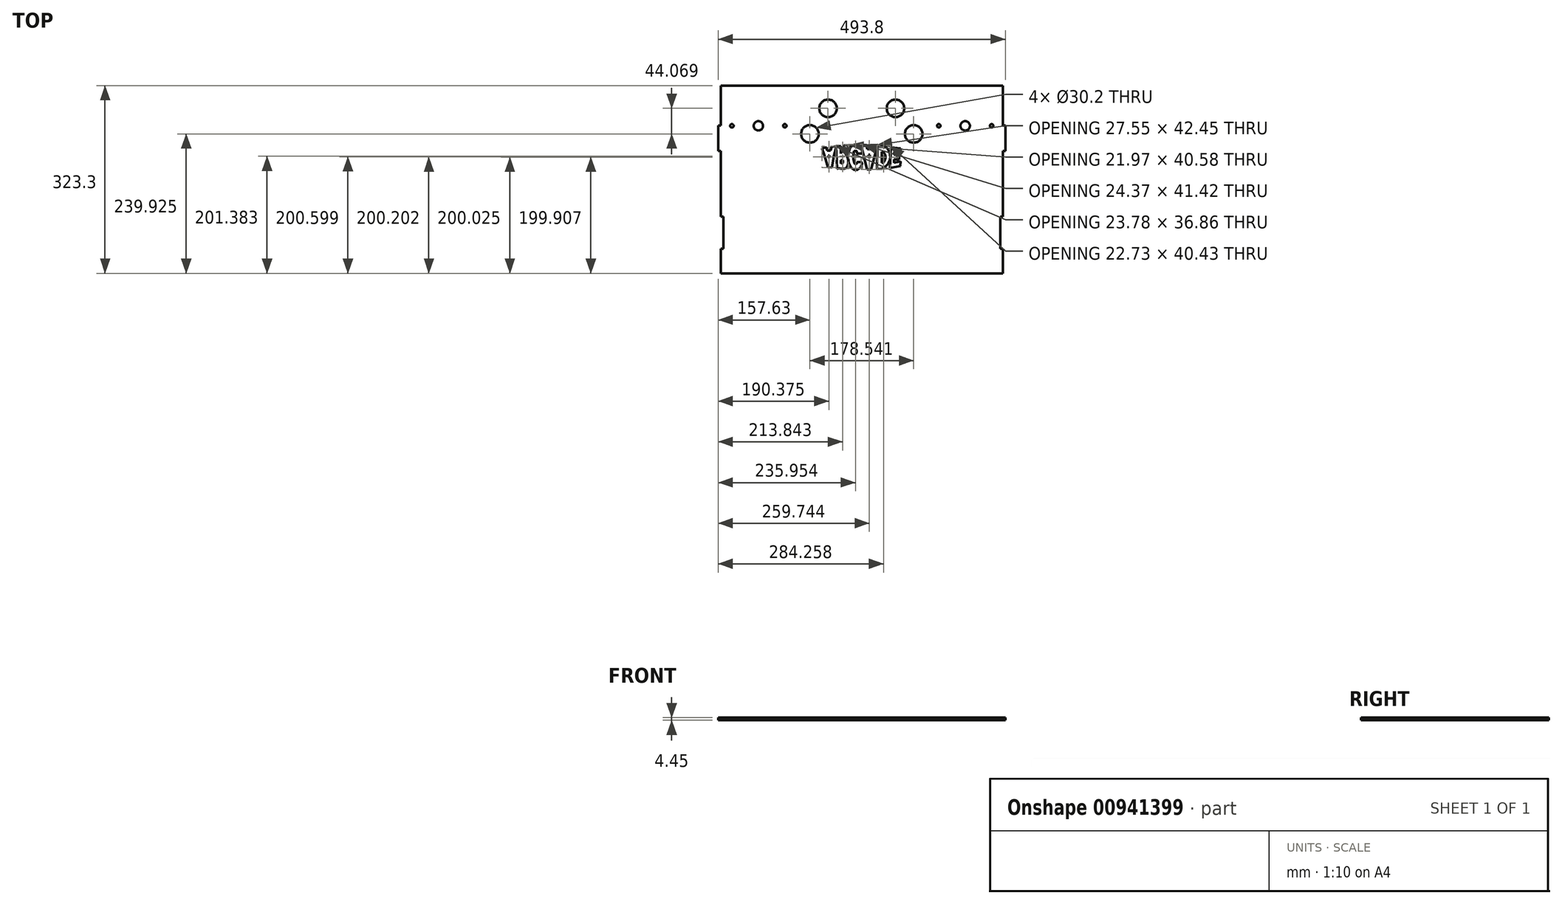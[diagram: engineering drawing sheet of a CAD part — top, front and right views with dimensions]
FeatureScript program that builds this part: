
annotation { "Feature Type Name" : "Feature", "Feature Type Description" : "" }
export const myFeature = defineFeature(function(context is Context, id is Id, definition is map)
    precondition{}
    {
        {
            var Q0;
            Q0=qCreatedBy(makeId("Top.planeOp"),FACE);
            var sketch = newSketch(context, id + "F0", { "sketchPlane" : qUnion([Q0])});
            skLineSegment(sketch, "E0.left", {"start": v(238, -33.63) * mm, "end": v(238, 22.07) * mm});
            skPoint(sketch, "E0.middle", {"position": v(0, 0) * mm});
            skLineSegment(sketch, "E1.bottom", {"start": v(238, 75.7) * mm, "end": v(242.45, 75.7) * mm});
            skLineSegment(sketch, "E1.top", {"start": v(238, 22.07) * mm, "end": v(242.45, 22.07) * mm});
            skLineSegment(sketch, "E1.right", {"start": v(242.45, 75.7) * mm, "end": v(242.45, 22.07) * mm});
            skLineSegment(sketch, "E2.bottom", {"start": v(238, -75.7) * mm, "end": v(242.45, -75.7) * mm});
            skLineSegment(sketch, "E2.top", {"start": v(238, -33.63) * mm, "end": v(242.45, -33.63) * mm});
            skLineSegment(sketch, "E2.right", {"start": v(242.45, -75.7) * mm, "end": v(242.45, -33.63) * mm});
            skLineSegment(sketch, "E3.left", {"start": v(238, 22.07) * mm, "end": v(238, -28.25) * mm});
            skLineSegment(sketch, "E4.MirrorCS", {"start": v(-242.45, -75.7) * mm, "end": v(-242.45, -33.63) * mm});
            skLineSegment(sketch, "E5.MirrorCS", {"start": v(-242.45, 75.7) * mm, "end": v(-242.45, 22.07) * mm});
            skLineSegment(sketch, "E6.MirrorCS", {"start": v(-238, 22.07) * mm, "end": v(-242.45, 22.07) * mm});
            skLineSegment(sketch, "E7.MirrorCS", {"start": v(-238, -33.63) * mm, "end": v(-238, 22.07) * mm});
            skLineSegment(sketch, "E8.MirrorCS", {"start": v(-238, -33.63) * mm, "end": v(-242.45, -33.63) * mm});
            skLineSegment(sketch, "E9.MirrorCS", {"start": v(-238, -75.7) * mm, "end": v(-242.45, -75.7) * mm});
            skLineSegment(sketch, "E10.MirrorCS", {"start": v(-238, 75.7) * mm, "end": v(-242.45, 75.7) * mm});
            skLineSegment(sketch, "E11.top", {"start": v(-232.45, 247.6) * mm, "end": v(232.45, 247.6) * mm});
            skLineSegment(sketch, "E11.left", {"start": v(-242.45, 75.7) * mm, "end": v(-242.45, 134.6) * mm});
            skLineSegment(sketch, "E11.right", {"start": v(242.45, 75.7) * mm, "end": v(242.45, 134.6) * mm});
            skPoint(sketch, "E12.visualSharp", {"position": v(-242.45, 247.6) * mm});
            skPoint(sketch, "E13.visualSharp", {"position": v(242.45, 247.6) * mm});
            skCircle(sketch, "E14", {"center": v(-223.33, 178.2) * mm, "radius": 3 * mm});
            skCircle(sketch, "E15", {"center": v(-132.43, 178.2) * mm, "radius": 3 * mm});
            skCircle(sketch, "E16", {"center": v(-89.27, 164.22) * mm, "radius": 15.1 * mm});
            skCircle(sketch, "E17", {"center": v(-58.02, 208.3) * mm, "radius": 15.1 * mm});
            skCircle(sketch, "E18.MirrorC", {"center": v(132.43, 178.2) * mm, "radius": 3 * mm});
            skCircle(sketch, "E19.MirrorC", {"center": v(223.33, 178.2) * mm, "radius": 3 * mm});
            skCircle(sketch, "E20.MirrorC", {"center": v(58.02, 208.3) * mm, "radius": 15.1 * mm});
            skCircle(sketch, "E21.MirrorC", {"center": v(89.27, 164.22) * mm, "radius": 15.1 * mm});
            skLineSegment(sketch, "E22.bottom", {"start": v(246.9, 134.6) * mm, "end": v(242.45, 134.6) * mm});
            skLineSegment(sketch, "E22.top", {"start": v(246.9, 178.7) * mm, "end": v(242.45, 178.7) * mm});
            skLineSegment(sketch, "E22.left", {"start": v(246.9, 134.6) * mm, "end": v(246.9, 178.7) * mm});
            skPoint(sketch, "E22.middle", {"position": v(242.45, 156.65) * mm});
            skPoint(sketch, "E22.right.start.orphan", {"position": v(238, 134.6) * mm});
            skLineSegment(sketch, "E23.trimOffspring", {"start": v(242.45, 178.7) * mm, "end": v(242.45, 237.6) * mm});
            skPoint(sketch, "E24.trimOffspring.end.orphan", {"position": v(238, 178.7) * mm});
            skLineSegment(sketch, "E25", {"start": v(-242.45, 237.6) * mm, "end": v(-242.45, 247.6) * mm});
            skLineSegment(sketch, "E26", {"start": v(-232.45, 247.6) * mm, "end": v(-242.45, 247.6) * mm});
            skLineSegment(sketch, "E27", {"start": v(232.45, 247.6) * mm, "end": v(242.45, 247.6) * mm});
            skLineSegment(sketch, "E28", {"start": v(242.45, 237.6) * mm, "end": v(242.45, 247.6) * mm});
            skLineSegment(sketch, "E29.MirrorCS", {"start": v(-246.9, 134.6) * mm, "end": v(-246.9, 178.7) * mm});
            skLineSegment(sketch, "E30.MirrorCS", {"start": v(-246.9, 134.6) * mm, "end": v(-242.45, 134.6) * mm});
            skLineSegment(sketch, "E31.MirrorCS", {"start": v(-246.9, 178.7) * mm, "end": v(-242.45, 178.7) * mm});
            skLineSegment(sketch, "E32.trimOffspring", {"start": v(-242.45, 178.7) * mm, "end": v(-242.45, 237.6) * mm});
            skLineSegment(sketch, "E33", {"start": v(-223.33, 178.2) * mm, "end": v(-220.33, 178.2) * mm});
            skCircle(sketch, "E34", {"center": v(-177.88, 178.2) * mm, "radius": 8.09 * mm});
            skLineSegment(sketch, "E35.trimOffspring", {"start": v(-135.43, 178.2) * mm, "end": v(-132.43, 178.2) * mm});
            skCircle(sketch, "E36.MirrorC", {"center": v(177.88, 178.2) * mm, "radius": 8.09 * mm});
            skLineSegment(sketch, "E37.MirrorCS", {"start": v(-36.17, 119.2) * mm, "end": v(-33.2, 119.2) * mm});
            skLineSegment(sketch, "E38.MirrorCS", {"start": v(26.62, 143.73) * mm, "end": v(26.56, 144.42) * mm});
            skLineSegment(sketch, "E39.MirrorCS", {"start": v(-0.93, 145.55) * mm, "end": v(-0.93, 145) * mm});
            skLineSegment(sketch, "E40.MirrorCS", {"start": v(-0.53, 145.55) * mm, "end": v(-0.93, 145.55) * mm});
            skLineSegment(sketch, "E41.MirrorCS", {"start": v(-32.23, 115.87) * mm, "end": v(-32.53, 114.75) * mm});
            skLineSegment(sketch, "E42.MirrorCS", {"start": v(-35.97, 113.5) * mm, "end": v(-36.17, 119.2) * mm});
            skLineSegment(sketch, "E43.MirrorCS", {"start": v(-32.1, 117.62) * mm, "end": v(-32.23, 115.87) * mm});
            skLineSegment(sketch, "E44.MirrorCS", {"start": v(-33.2, 119.2) * mm, "end": v(-32.1, 117.62) * mm});
            skLineSegment(sketch, "E45.MirrorCS", {"start": v(-33.2, 113.84) * mm, "end": v(-35.97, 113.5) * mm});
            skLineSegment(sketch, "E46.MirrorCS", {"start": v(-32.53, 114.75) * mm, "end": v(-33.2, 113.84) * mm});
            skLineSegment(sketch, "E47.MirrorCS", {"start": v(-23.7, 120.7) * mm, "end": v(-23.63, 120.17) * mm});
            skLineSegment(sketch, "E48.MirrorCS", {"start": v(-60.29, 140.96) * mm, "end": v(-60.29, 138.53) * mm});
            skLineSegment(sketch, "E49.MirrorCS", {"start": v(-53.54, 135.83) * mm, "end": v(-52.35, 139.61) * mm});
            skLineSegment(sketch, "E50.MirrorCS", {"start": v(-52.35, 139.61) * mm, "end": v(-52.35, 141.88) * mm});
            skLineSegment(sketch, "E51.MirrorCS", {"start": v(-60.29, 138.53) * mm, "end": v(-59.7, 135.3) * mm});
            skLineSegment(sketch, "E52.MirrorCS", {"start": v(-59.7, 135.3) * mm, "end": v(-53.54, 135.83) * mm});
            skLineSegment(sketch, "E53.MirrorCS", {"start": v(-44.64, 140.15) * mm, "end": v(-44.64, 143.33) * mm});
            skLineSegment(sketch, "E54.MirrorCS", {"start": v(-27.9, 128.28) * mm, "end": v(-26.01, 126.06) * mm});
            skLineSegment(sketch, "E55.MirrorCS", {"start": v(-44.64, 143.33) * mm, "end": v(-52.35, 141.88) * mm});
            skLineSegment(sketch, "E56.MirrorCS", {"start": v(14.2, 128.31) * mm, "end": v(12.9, 122.55) * mm});
            skLineSegment(sketch, "E57.MirrorCS", {"start": v(55.58, 128.77) * mm, "end": v(64.18, 127.53) * mm});
            skLineSegment(sketch, "E58.MirrorCS", {"start": v(27.1, 144.42) * mm, "end": v(38.2, 143.73) * mm});
            skLineSegment(sketch, "E59.MirrorCS", {"start": v(8.88, 103.1) * mm, "end": v(15.8, 103.1) * mm});
            skLineSegment(sketch, "E60.MirrorCS", {"start": v(-31.26, 144.14) * mm, "end": v(-22.07, 144.8) * mm});
            skLineSegment(sketch, "E61.MirrorCS", {"start": v(66.58, 116.97) * mm, "end": v(66.01, 108.94) * mm});
            skLineSegment(sketch, "E62.MirrorCS", {"start": v(12.9, 122.55) * mm, "end": v(11.59, 128.31) * mm});
            skLineSegment(sketch, "E63.MirrorCS", {"start": v(8.38, 145.02) * mm, "end": v(-0.53, 145.55) * mm});
            skLineSegment(sketch, "E64.MirrorCS", {"start": v(64.18, 127.53) * mm, "end": v(64.18, 120.34) * mm});
            skLineSegment(sketch, "E65.MirrorCS", {"start": v(-31.57, 142.58) * mm, "end": v(-31.26, 144.14) * mm});
            skLineSegment(sketch, "E66.MirrorCS", {"start": v(36.8, 114.75) * mm, "end": v(34.67, 114.75) * mm});
            skLineSegment(sketch, "E67.MirrorCS", {"start": v(-44.04, 143.12) * mm, "end": v(-36.1, 143.4) * mm});
            skLineSegment(sketch, "E68.MirrorCS", {"start": v(-67.69, 137.61) * mm, "end": v(-68.41, 139.34) * mm});
            skLineSegment(sketch, "E69.MirrorCS", {"start": v(66.76, 131.65) * mm, "end": v(56.22, 133.17) * mm});
            skLineSegment(sketch, "E70.MirrorCS", {"start": v(17.44, 142.14) * mm, "end": v(16.43, 137.85) * mm});
            skLineSegment(sketch, "E71.MirrorCS", {"start": v(8.38, 142.78) * mm, "end": v(8.38, 145.02) * mm});
            skLineSegment(sketch, "E72.MirrorCS", {"start": v(26, 104) * mm, "end": v(34.24, 104.65) * mm});
            skLineSegment(sketch, "E73.MirrorCS", {"start": v(64.18, 120.34) * mm, "end": v(55.31, 120.34) * mm});
            skLineSegment(sketch, "E74.MirrorCS", {"start": v(56.22, 133.17) * mm, "end": v(55.58, 128.77) * mm});
            skLineSegment(sketch, "E75.MirrorCS", {"start": v(-56.33, 123.14) * mm, "end": v(-57.66, 127.36) * mm});
            skLineSegment(sketch, "E76.MirrorCS", {"start": v(9.64, 137.85) * mm, "end": v(8.38, 142.78) * mm});
            skLineSegment(sketch, "E77.MirrorCS", {"start": v(-55.5, 127.36) * mm, "end": v(-56.33, 123.14) * mm});
            skLineSegment(sketch, "E78.MirrorCS", {"start": v(17.44, 144.42) * mm, "end": v(17.44, 142.14) * mm});
            skLineSegment(sketch, "E79.MirrorCS", {"start": v(16.43, 137.85) * mm, "end": v(9.64, 137.85) * mm});
            skLineSegment(sketch, "E80.MirrorCS", {"start": v(34.67, 133.45) * mm, "end": v(37.31, 133.17) * mm});
            skLineSegment(sketch, "E81.MirrorCS", {"start": v(-68.41, 139.34) * mm, "end": v(-60.29, 140.96) * mm});
            skLineSegment(sketch, "E82.MirrorCS", {"start": v(-51.55, 106.47) * mm, "end": v(-58.02, 107.17) * mm});
            skLineSegment(sketch, "E83.MirrorCS", {"start": v(-57.66, 127.36) * mm, "end": v(-55.5, 127.36) * mm});
            skLineSegment(sketch, "E84.MirrorCS", {"start": v(55.31, 120.34) * mm, "end": v(55.31, 114.75) * mm});
            skLineSegment(sketch, "E85.MirrorCS", {"start": v(11.59, 128.31) * mm, "end": v(14.2, 128.31) * mm});
            skLineSegment(sketch, "E86.MirrorCS", {"start": v(-66.23, 132.49) * mm, "end": v(-67.69, 137.61) * mm});
            skLineSegment(sketch, "E87.MirrorCS", {"start": v(55.31, 114.75) * mm, "end": v(66.58, 116.97) * mm});
            skLineSegment(sketch, "E88.MirrorCS", {"start": v(66.76, 139.2) * mm, "end": v(66.76, 131.65) * mm});
            skLineSegment(sketch, "E89.MirrorCS", {"start": v(26.56, 144.42) * mm, "end": v(17.44, 144.42) * mm});
            skFitSpline(sketch, "E90.MirrorC", {"points": [v(-8.4, 115.9) * mm, v(-8.55, 114.1) * mm, v(-9.41, 112.4) * mm, v(-10.98, 112.06) * mm, v(-12.6, 113.42) * mm, v(-14.48, 119.42) * mm, v(-14.83, 125.98) * mm, v(-14.02, 132.21) * mm, v(-12.1, 135.5) * mm, v(-9.77, 135.83) * mm, v(-8.7, 133.23) * mm, v(-7.74, 130.17) * mm, v(-6.93, 130.17) * mm, v(0, 130.12) * mm, v(1.22, 130.17) * mm, v(-1, 140.36) * mm, v(-1.42, 141.04) * mm, v(-5.2, 145.46) * mm, v(-13.31, 145.8) * mm, v(-18.28, 142.85) * mm, v(-22.12, 135.27) * mm, v(-23.29, 124.17) * mm, v(-21.72, 112.51) * mm, v(-18.12, 105.94) * mm, v(-14.22, 102.55) * mm, v(-9.72, 102.04) * mm, v(-4.75, 103.68) * mm, v(-0.6, 109.51) * mm, v(0.92, 114.78) * mm, v(0.97, 115.9) * mm, v(-1.42, 116.13) * mm, v(-8.4, 115.9) * mm]});
            skFitSpline(sketch, "E91.MirrorCS", {"points": [v(-26.01, 126.06) * mm, v(-23.7, 120.7) * mm, v(-23.7, 112.15) * mm, v(-28.69, 104.61) * mm, v(-39.94, 104.84) * mm, v(-42.7, 104.96) * mm, v(-30.02, 128.86) * mm, v(-26.01, 126.06) * mm]});
            skLineSegment(sketch, "E92.MirrorCS", {"start": v(-22.07, 144.8) * mm, "end": v(-27.9, 128.28) * mm});
            skArc(sketch, "E93.MirrorCS", {"start": v(37.31, 133.17) * mm, "mid": v(40.93, 123.86) * mm, "end": v(36.8, 114.75) * mm});
            skLineSegment(sketch, "E94.MirrorCS", {"start": v(15.8, 103.1) * mm, "end": v(26.62, 143.73) * mm});
            skLineSegment(sketch, "E95.MirrorCS", {"start": v(-58.02, 107.17) * mm, "end": v(-62.34, 120.5) * mm});
            skLineSegment(sketch, "E96.MirrorCS", {"start": v(-42.7, 104.96) * mm, "end": v(-44.04, 143.12) * mm});
            skLineSegment(sketch, "E97.MirrorCS", {"start": v(-0.93, 145) * mm, "end": v(8.88, 103.1) * mm});
            skLineSegment(sketch, "E98.MirrorCS", {"start": v(48.25, 105.78) * mm, "end": v(50.6, 141.48) * mm});
            skLineSegment(sketch, "E99.MirrorCS", {"start": v(-62.34, 120.5) * mm, "end": v(-66.23, 132.49) * mm});
            skLineSegment(sketch, "E100.MirrorCS", {"start": v(26, 104) * mm, "end": v(27.1, 144.42) * mm});
            skLineSegment(sketch, "E101.MirrorCS", {"start": v(50.6, 141.48) * mm, "end": v(66.76, 139.2) * mm});
            skLineSegment(sketch, "E102.MirrorCS", {"start": v(-36.1, 130.22) * mm, "end": v(-31.57, 142.58) * mm});
            skLineSegment(sketch, "E103.MirrorCS", {"start": v(-36.1, 143.4) * mm, "end": v(-36.1, 130.22) * mm});
            skLineSegment(sketch, "E104.MirrorCS", {"start": v(-44.64, 140.15) * mm, "end": v(-48.2, 126.06) * mm});
            skLineSegment(sketch, "E105.MirrorCS", {"start": v(34.67, 114.75) * mm, "end": v(34.67, 133.45) * mm});
            skLineSegment(sketch, "E106.MirrorCS", {"start": v(66.01, 108.94) * mm, "end": v(48.25, 105.78) * mm});
            skArc(sketch, "E107.MirrorCS", {"start": v(38.2, 143.73) * mm, "mid": v(48.72, 122.93) * mm, "end": v(34.24, 104.65) * mm});
            skLineSegment(sketch, "E108.MirrorCS", {"start": v(-48.2, 126.06) * mm, "end": v(-51.55, 106.47) * mm});
            skLineSegment(sketch, "E109", {"start": v(-238, -75.7) * mm, "end": v(238, -75.7) * mm});
            skSolve(sketch);
        }
        {
            var Q0;
            Q0=makeQuery(id+"F0.imprint","IMPRINT",FACE,{"disambiguationData":[TD([[makeQuery(id+"F0.imprint","IMPRINT",EDGE,{"derivedFrom":sQuery(id+"F0.wireOp",EDGE,"E0.left")}),1.0]])]});
            var Q1;
            Q1=makeQuery(id+"F0.imprint","IMPRINT",FACE,{"disambiguationData":[TD([[makeQuery(id+"F0.imprint","IMPRINT",EDGE,{"derivedFrom":sQuery(id+"F0.wireOp",EDGE,"E75.MirrorCS")}),-1.0]])]});
            var Q2;
            Q2=makeQuery(id+"F0.imprint","IMPRINT",FACE,{"disambiguationData":[TD([[makeQuery(id+"F0.imprint","IMPRINT",EDGE,{"derivedFrom":sQuery(id+"F0.wireOp",EDGE,"E37.MirrorCS")}),-1.0]])]});
            var Q3;
            Q3=makeQuery(id+"F0.imprint","IMPRINT",FACE,{"disambiguationData":[TD([[makeQuery(id+"F0.imprint","IMPRINT",EDGE,{"derivedFrom":sQuery(id+"F0.wireOp",EDGE,"E56.MirrorCS")}),-1.0]])]});
            var Q4;
            Q4=makeQuery(id+"F0.imprint","IMPRINT",FACE,{"disambiguationData":[TD([[makeQuery(id+"F0.imprint","IMPRINT",EDGE,{"derivedFrom":sQuery(id+"F0.wireOp",EDGE,"E66.MirrorCS")}),-1.0]])]});
            extrude(context, id + "F1", {"entities" : qUnion([Q0, Q1, Q2, Q3, Q4]), "depth" : 4.45 * mm, "offsetDistance" : 25 * mm});
        }
    });
